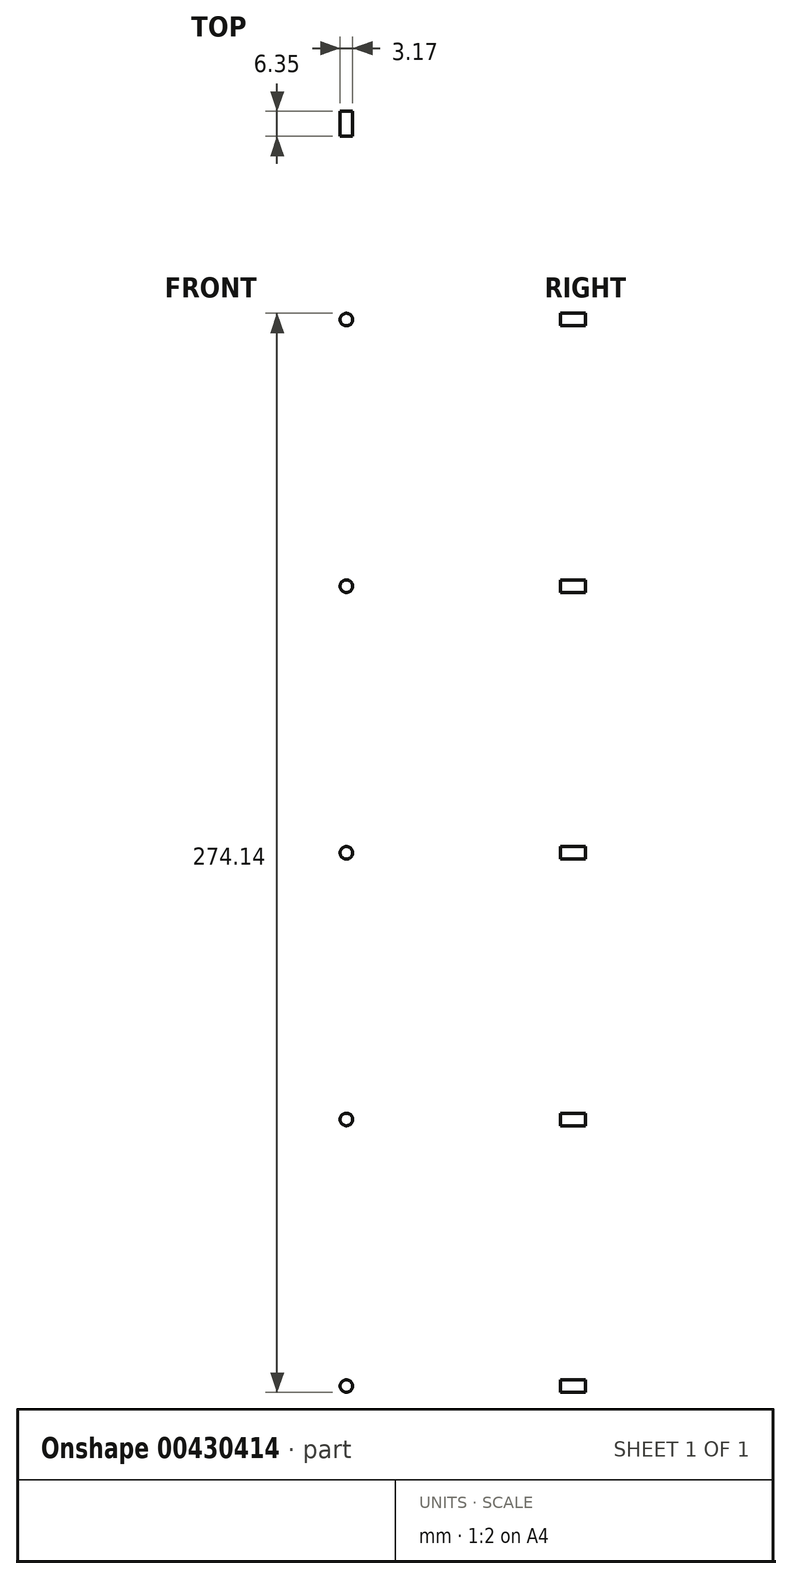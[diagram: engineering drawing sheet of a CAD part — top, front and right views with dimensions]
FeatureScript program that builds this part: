
annotation { "Feature Type Name" : "Feature", "Feature Type Description" : "" }
export const myFeature = defineFeature(function(context is Context, id is Id, definition is map)
    precondition{}
    {
        {
            var Q0;
            Q0=qCreatedBy(makeId("Front.planeOp"),FACE);
            var sketch = newSketch(context, id + "F0", { "sketchPlane" : qUnion([Q0])});
            skLineSegment(sketch, "E0.bottom", {"start": v(247.65, -198.44) * mm, "end": v(-247.65, -198.44) * mm});
            skLineSegment(sketch, "E0.top", {"start": v(247.65, 198.44) * mm, "end": v(-247.65, 198.44) * mm});
            skLineSegment(sketch, "E0.left", {"start": v(247.65, -198.44) * mm, "end": v(247.65, 198.44) * mm});
            skLineSegment(sketch, "E0.right", {"start": v(-247.65, -198.44) * mm, "end": v(-247.65, 198.44) * mm});
            skPoint(sketch, "E0.middle", {"position": v(0, 0) * mm});
            skSolve(sketch);
        }
        {
            var Q0;
            Q0=makeQuery(id+"F0.imprint","IMPRINT",FACE,{"disambiguationData":[TD([[makeQuery(id+"F0.imprint","IMPRINT",EDGE,{"derivedFrom":sQuery(id+"F0.wireOp",EDGE,"E0.bottom")}),-1.0]])]});
            extrude(context, id + "F1", {"entities" : qUnion([Q0]), "depth" : 6.35 * mm, "offsetDistance" : 25.4 * mm});
        }
        {
            var Q0;
            Q0=makeQuery(id+"F1.opExtrude","CAP_FACE",FACE,{"disambiguationData":[OSD([sQuery(id+"F0.wireOp",EDGE,"E0.bottom"),sQuery(id+"F0.wireOp",EDGE,"E0.top"),sQuery(id+"F0.wireOp",EDGE,"E0.left"),sQuery(id+"F0.wireOp",EDGE,"E0.right")])],"isStart":false});
            var sketch = newSketch(context, id + "F2", { "sketchPlane" : qUnion([Q0])});
            skLineSegment(sketch, "E1", {"start": v(-242.77, 198.44) * mm, "end": v(-242.77, -198.44) * mm, "construction": true});
            skCircle(sketch, "E2", {"center": v(-242.77, 130.7) * mm, "radius": 1.59 * mm});
            skCircle(sketch, "E3.0.1.0", {"center": v(-242.77, 62.95) * mm, "radius": 1.59 * mm});
            skCircle(sketch, "E3.0.2.0", {"center": v(-242.77, -4.79) * mm, "radius": 1.59 * mm});
            skCircle(sketch, "E3.0.3.0", {"center": v(-242.77, -72.53) * mm, "radius": 1.59 * mm});
            skCircle(sketch, "E3.0.4.0", {"center": v(-242.77, -140.27) * mm, "radius": 1.59 * mm});
            skLineSegment(sketch, "E3.direction1", {"start": v(-242.77, 130.7) * mm, "end": v(-209.55, 130.7) * mm, "construction": true});
            skLineSegment(sketch, "E3.direction2", {"start": v(-242.77, 130.7) * mm, "end": v(-242.77, 62.95) * mm, "construction": true});
            skLineSegment(sketch, "E4", {"start": v(0, 198.44) * mm, "end": v(0, -198.44) * mm, "construction": true});
            skCircle(sketch, "E5.MirrorC", {"center": v(242.77, 130.7) * mm, "radius": 1.59 * mm});
            skCircle(sketch, "E6.MirrorC", {"center": v(242.77, 62.95) * mm, "radius": 1.59 * mm});
            skCircle(sketch, "E7.MirrorC", {"center": v(242.77, -4.79) * mm, "radius": 1.59 * mm});
            skCircle(sketch, "E8.MirrorC", {"center": v(242.77, -72.53) * mm, "radius": 1.59 * mm});
            skCircle(sketch, "E9.MirrorC", {"center": v(242.77, -140.27) * mm, "radius": 1.59 * mm});
            skSolve(sketch);
        }
        {
            var Q0;
            Q0=makeQuery(id+"F2.imprint","IMPRINT",FACE,{"disambiguationData":[TD([[makeQuery(id+"F2.imprint","IMPRINT",EDGE,{"derivedFrom":sQuery(id+"F2.wireOp",EDGE,"E2")}),1.0]])]});
            var Q1;
            Q1=makeQuery(id+"F2.imprint","IMPRINT",FACE,{"disambiguationData":[TD([[makeQuery(id+"F2.imprint","IMPRINT",EDGE,{"derivedFrom":sQuery(id+"F2.wireOp",EDGE,"E3.0.1.0")}),1.0]])]});
            var Q2;
            Q2=makeQuery(id+"F2.imprint","IMPRINT",FACE,{"disambiguationData":[TD([[makeQuery(id+"F2.imprint","IMPRINT",EDGE,{"derivedFrom":sQuery(id+"F2.wireOp",EDGE,"E3.0.2.0")}),1.0]])]});
            var Q3;
            Q3=makeQuery(id+"F2.imprint","IMPRINT",FACE,{"disambiguationData":[TD([[makeQuery(id+"F2.imprint","IMPRINT",EDGE,{"derivedFrom":sQuery(id+"F2.wireOp",EDGE,"E3.0.3.0")}),1.0]])]});
            var Q4;
            Q4=makeQuery(id+"F2.imprint","IMPRINT",FACE,{"disambiguationData":[TD([[makeQuery(id+"F2.imprint","IMPRINT",EDGE,{"derivedFrom":sQuery(id+"F2.wireOp",EDGE,"E3.0.4.0")}),1.0]])]});
            var Q5;
            Q5=makeQuery(id+"F2.imprint","IMPRINT",FACE,{"disambiguationData":[TD([[makeQuery(id+"F2.imprint","IMPRINT",EDGE,{"derivedFrom":sQuery(id+"F2.wireOp",EDGE,"E5.MirrorC")}),-1.0]])]});
            var Q6;
            Q6=makeQuery(id+"F2.imprint","IMPRINT",FACE,{"disambiguationData":[TD([[makeQuery(id+"F2.imprint","IMPRINT",EDGE,{"derivedFrom":sQuery(id+"F2.wireOp",EDGE,"E6.MirrorC")}),-1.0]])]});
            var Q7;
            Q7=makeQuery(id+"F2.imprint","IMPRINT",FACE,{"disambiguationData":[TD([[makeQuery(id+"F2.imprint","IMPRINT",EDGE,{"derivedFrom":sQuery(id+"F2.wireOp",EDGE,"E7.MirrorC")}),-1.0]])]});
            var Q8;
            Q8=makeQuery(id+"F2.imprint","IMPRINT",FACE,{"disambiguationData":[TD([[makeQuery(id+"F2.imprint","IMPRINT",EDGE,{"derivedFrom":sQuery(id+"F2.wireOp",EDGE,"E8.MirrorC")}),-1.0]])]});
            var Q9;
            Q9=makeQuery(id+"F2.imprint","IMPRINT",FACE,{"disambiguationData":[TD([[makeQuery(id+"F2.imprint","IMPRINT",EDGE,{"derivedFrom":sQuery(id+"F2.wireOp",EDGE,"E9.MirrorC")}),-1.0]])]});
            extrude(context, id + "F3", {"entities" : qUnion([Q0, Q1, Q2, Q3, Q4, Q5, Q6, Q7, Q8, Q9]), "operationType" : NewBodyOperationType.REMOVE, "oppositeDirection" : true, "depth" : 25.4 * mm, "offsetDistance" : 25.4 * mm});
        }
    });
